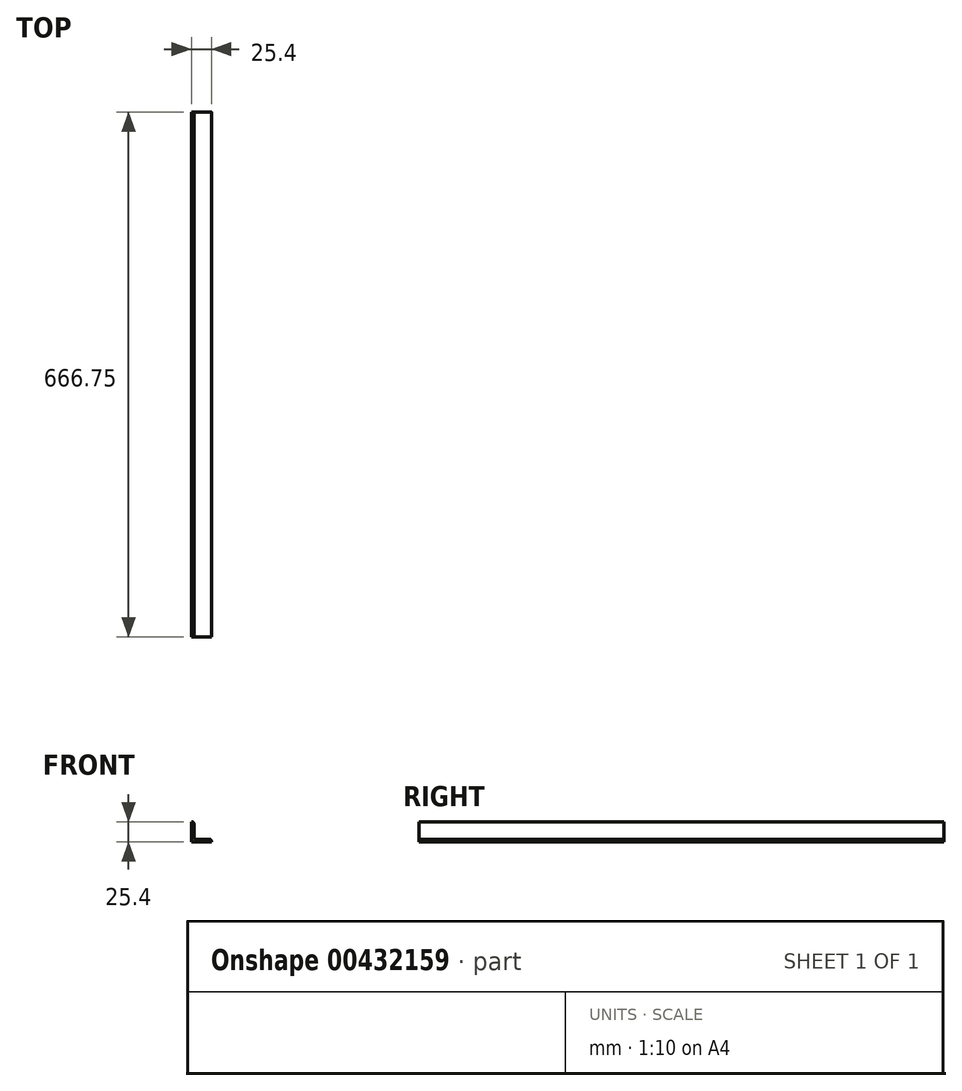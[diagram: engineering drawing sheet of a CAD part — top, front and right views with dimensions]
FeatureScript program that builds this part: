
annotation { "Feature Type Name" : "Feature", "Feature Type Description" : "" }
export const myFeature = defineFeature(function(context is Context, id is Id, definition is map)
    precondition{}
    {
        {
            var Q0;
            Q0=qCreatedBy(makeId("Front.planeOp"),FACE);
            var sketch = newSketch(context, id + "F0", { "sketchPlane" : qUnion([Q0])});
            skLineSegment(sketch, "E0", {"start": v(0, 0) * mm, "end": v(0, 25.4) * mm});
            skLineSegment(sketch, "E1", {"start": v(0, 0) * mm, "end": v(25.4, 0) * mm});
            skLineSegment(sketch, "E2", {"start": v(25.4, 0) * mm, "end": v(25.4, 0.79) * mm});
            skLineSegment(sketch, "E3", {"start": v(23.01, 3.18) * mm, "end": v(6.35, 3.17) * mm});
            skLineSegment(sketch, "E4", {"start": v(3.18, 6.35) * mm, "end": v(3.18, 23.01) * mm});
            skLineSegment(sketch, "E5", {"start": v(0.79, 25.4) * mm, "end": v(0, 25.4) * mm});
            skPoint(sketch, "E6.visualSharp", {"position": v(3.18, 25.4) * mm});
            skArc(sketch, "E6.filletArc", {"start": v(3.18, 23.01) * mm, "mid": v(2.48, 24.7) * mm, "end": v(0.79, 25.4) * mm});
            skPoint(sketch, "E7.visualSharp", {"position": v(25.4, 3.18) * mm});
            skArc(sketch, "E7.filletArc", {"start": v(25.4, 0.79) * mm, "mid": v(24.7, 2.48) * mm, "end": v(23.01, 3.18) * mm});
            skPoint(sketch, "E8.visualSharp", {"position": v(3.18, 3.17) * mm});
            skArc(sketch, "E8.filletArc", {"start": v(3.17, 6.35) * mm, "mid": v(4.1, 4.1) * mm, "end": v(6.35, 3.17) * mm});
            skLineSegment(sketch, "E9", {"start": v(1.37, 25.83) * mm, "end": v(28.8, -1.62) * mm, "construction": true});
            skPoint(sketch, "E10", {"position": v(13.6, 13.59) * mm});
            skSolve(sketch);
        }
        {
            var Q0;
            Q0=makeQuery(id+"F0.imprint","IMPRINT",FACE,{"disambiguationData":[TD([[makeQuery(id+"F0.imprint","IMPRINT",EDGE,{"derivedFrom":sQuery(id+"F0.wireOp",EDGE,"E0")}),-1.0]])]});
            extrude(context, id + "F1", {"entities" : qUnion([Q0]), "depth" : 666.75 * mm});
        }
    });
